# Revit family: Haworth_Masters_ConvergentWorktop-Wedge
name_source: partatom
category: Furniture Systems
revit_build: Autodesk Revit 2018 (Build: 20170223_1515(x64)
units: mm (PartAtom-declared; Revit-internal decimal feet)

## family parameters
Always vertical = Yes
Cut with Voids When Loaded = No
OmniClass Number = 23.40.70.14.64.21
OmniClass Title = Systems Furniture
Part Type = Normal
Room Calculation Point = No
Round Connector Dimension = Use Diameter
Shared = No
Work Plane-Based = No

## types (27) — shared parameters
Actual Height = 30"
Assembly Code = E2020200
Custom Size = No
Height = 30"
Leg Finish = Haworth _ Paint _ Metallic Champagne
Manufacturer = Haworth
Min. Height = 28 11/16"
Min/Max Height = 28 11/16-32 11/16 in.
Model = Masters
Revision Number = 1
Size = Verify Final Dim. w/ Haworth
Support Height = 28 13/16"
Support Offset = 1 1/4"
Sustainability Info = http://media.haworth.com
URL = http://www.haworth.com
URL - Product = http://www.haworth.com
Warranty = http://www.haworth.com
Worksurface Thickness = 1 3/16"

## per-type parameters (varying)
| type | Actual Depth | Actual Support Depth | Actual Width | Depth | Height Adjustable | Hoop Leg | Max. Depth | Max. Height | Max. Width | Min. Depth | Min. Width | Min/Max Depth | Min/Max Width | Support Column | Width |
| 41d 58w - Wedge Radius - Height Adjustable | 41" | 32 1/2" | 58" | 41" | Yes | No | 47" | 47 3/16" | 82" | 41" | 58" | 41,47 in. | 58-82 in. @ 6 in. Increments | No | 58" |
| 41d 64w - Wedge Radius - Height Adjustable | 41" | 32 1/2" | 64" | 41" | Yes | No | 47" | 47 3/16" | 82" | 41" | 58" | 41,47 in. | 58-82 in. @ 6 in. Increments | No | 64" |
| 41d 70w - Wedge Radius - Height Adjustable | 41" | 32 1/2" | 70" | 41" | Yes | No | 47" | 47 3/16" | 82" | 41" | 58" | 41,47 in. | 58-82 in. @ 6 in. Increments | No | 70" |
| 41d 76w - Wedge Radius - Height Adjustable | 41" | 32 1/2" | 76" | 41" | Yes | No | 47" | 47 3/16" | 82" | 41" | 58" | 41,47 in. | 58-82 in. @ 6 in. Increments | No | 76" |
| 41d 82w - Wedge Radius - Height Adjustable | 41" | 32 1/2" | 82" | 41" | Yes | No | 47" | 47 3/16" | 82" | 41" | 58" | 41,47 in. | 58-82 in. @ 6 in. Increments | No | 82" |
| 47d 58w - Wedge Radius - Height Adjustable | 47" | 38 1/2" | 58" | 47" | Yes | No | 47" | 47 3/16" | 82" | 41" | 58" | 41,47 in. | 58-82 in. @ 6 in. Increments | No | 58" |
| 47d 64w - Wedge Radius - Height Adjustable | 47" | 38 1/2" | 64" | 47" | Yes | No | 47" | 47 3/16" | 82" | 41" | 58" | 41,47 in. | 58-82 in. @ 6 in. Increments | No | 64" |
| 47d 70w - Wedge Radius - Height Adjustable | 47" | 38 1/2" | 70" | 47" | Yes | No | 47" | 47 3/16" | 82" | 41" | 58" | 41,47 in. | 58-82 in. @ 6 in. Increments | No | 70" |
| 47d 76w - Wedge Radius - Height Adjustable | 47" | 38 1/2" | 76" | 47" | Yes | No | 47" | 47 3/16" | 82" | 41" | 58" | 41,47 in. | 58-82 in. @ 6 in. Increments | No | 76" |
| 47d 82w - Wedge Radius - Height Adjustable | 47" | 38 1/2" | 82" | 47" | Yes | No | 47" | 47 3/16" | 82" | 41" | 58" | 41,47 in. | 58-82 in. @ 6 in. Increments | No | 82" |
| 42d 60w - Wedge Radius - Column | 42" | 33 1/2" | 60" | 42" | No | No | 48" | 32 11/16" | 84" | 42" | 60" | 42,48 in. | 60-84 in. @ 6 in. Increments | Yes | 60" |
| 42d 66w - Wedge Radius - Column | 42" | 33 1/2" | 66" | 42" | No | No | 48" | 32 11/16" | 84" | 42" | 60" | 42,48 in. | 60-84 in. @ 6 in. Increments | Yes | 66" |
| 42d 72w - Wedge Radius - Column | 42" | 33 1/2" | 72" | 42" | No | No | 48" | 32 11/16" | 84" | 42" | 60" | 42,48 in. | 60-84 in. @ 6 in. Increments | Yes | 72" |
| 42d 78w - Wedge Radius - Column | 42" | 33 1/2" | 78" | 42" | No | No | 48" | 32 11/16" | 84" | 42" | 60" | 42,48 in. | 60-84 in. @ 6 in. Increments | Yes | 78" |
| 42d 84w - Wedge Radius - Column | 42" | 33 1/2" | 84" | 42" | No | No | 48" | 32 11/16" | 84" | 42" | 60" | 42,48 in. | 60-84 in. @ 6 in. Increments | Yes | 84" |
| 48d 60w - Wedge Radius - Column | 48" | 39 1/2" | 60" | 48" | No | No | 48" | 32 11/16" | 84" | 42" | 60" | 42,48 in. | 60-84 in. @ 6 in. Increments | Yes | 60" |
| 48d 66w - Wedge Radius - Column | 48" | 39 1/2" | 66" | 48" | No | No | 48" | 32 11/16" | 84" | 42" | 60" | 42,48 in. | 60-84 in. @ 6 in. Increments | Yes | 66" |
| 48d 72w - Wedge Radius - Column | 48" | 39 1/2" | 72" | 48" | No | No | 48" | 32 11/16" | 84" | 42" | 60" | 42,48 in. | 60-84 in. @ 6 in. Increments | Yes | 72" |
| 48d 78w - Wedge Radius - Column | 48" | 39 1/2" | 78" | 48" | No | No | 48" | 32 11/16" | 84" | 42" | 60" | 42,48 in. | 60-84 in. @ 6 in. Increments | Yes | 78" |
| 48d 84w - Wedge Radius - Column | 48" | 39 1/2" | 84" | 48" | No | No | 48" | 32 11/16" | 84" | 42" | 60" | 42,48 in. | 60-84 in. @ 6 in. Increments | Yes | 84" |
| 42d 60w - Wedge Radius - Hoop | 42" | 33 1/2" | 60" | 42" | No | Yes | 48" | 32 11/16" | 84" | 42" | 60" | 42,48 in. | 60-84 in. @ 6 in. Increments | No | 60" |
| 42d 66w - Wedge Radius - Hoop | 42" | 33 1/2" | 66" | 42" | No | Yes | 48" | 32 11/16" | 84" | 42" | 60" | 42,48 in. | 60-84 in. @ 6 in. Increments | No | 66" |
| 42d 72w - Wedge Radius - Hoop | 48" | 39 1/2" | 72" | 48" | No | Yes | 48" | 32 11/16" | 84" | 42" | 60" | 42,48 in. | 60-84 in. @ 6 in. Increments | No | 72" |
| 42d 78w - Wedge Radius - Hoop | 48" | 39 1/2" | 78" | 48" | No | Yes | 48" | 32 11/16" | 84" | 42" | 60" | 42,48 in. | 60-84 in. @ 6 in. Increments | No | 78" |
| 42d 84w - Wedge Radius - Hoop | 48" | 39 1/2" | 84" | 48" | No | Yes | 48" | 32 11/16" | 84" | 42" | 60" | 42,48 in. | 60-84 in. @ 6 in. Increments | No | 84" |
| 36d 60w - Wedge Radius - Hoop | 48" | 39 1/2" | 60" | 48" | No | Yes | 48" | 32 11/16" | 84" | 42" | 60" | 42,48 in. | 60-84 in. @ 6 in. Increments | No | 60" |
| 36d 66w - Wedge Radius - Hoop | 48" | 39 1/2" | 66" | 48" | No | Yes | 48" | 32 11/16" | 84" | 42" | 60" | 42,48 in. | 60-84 in. @ 6 in. Increments | No | 66" |

note: column(s) folded — value = type name in every type: Description

## geometry (parser evidence)
native form markers: Sweep x12
no freeform markers — native parametric forms only
